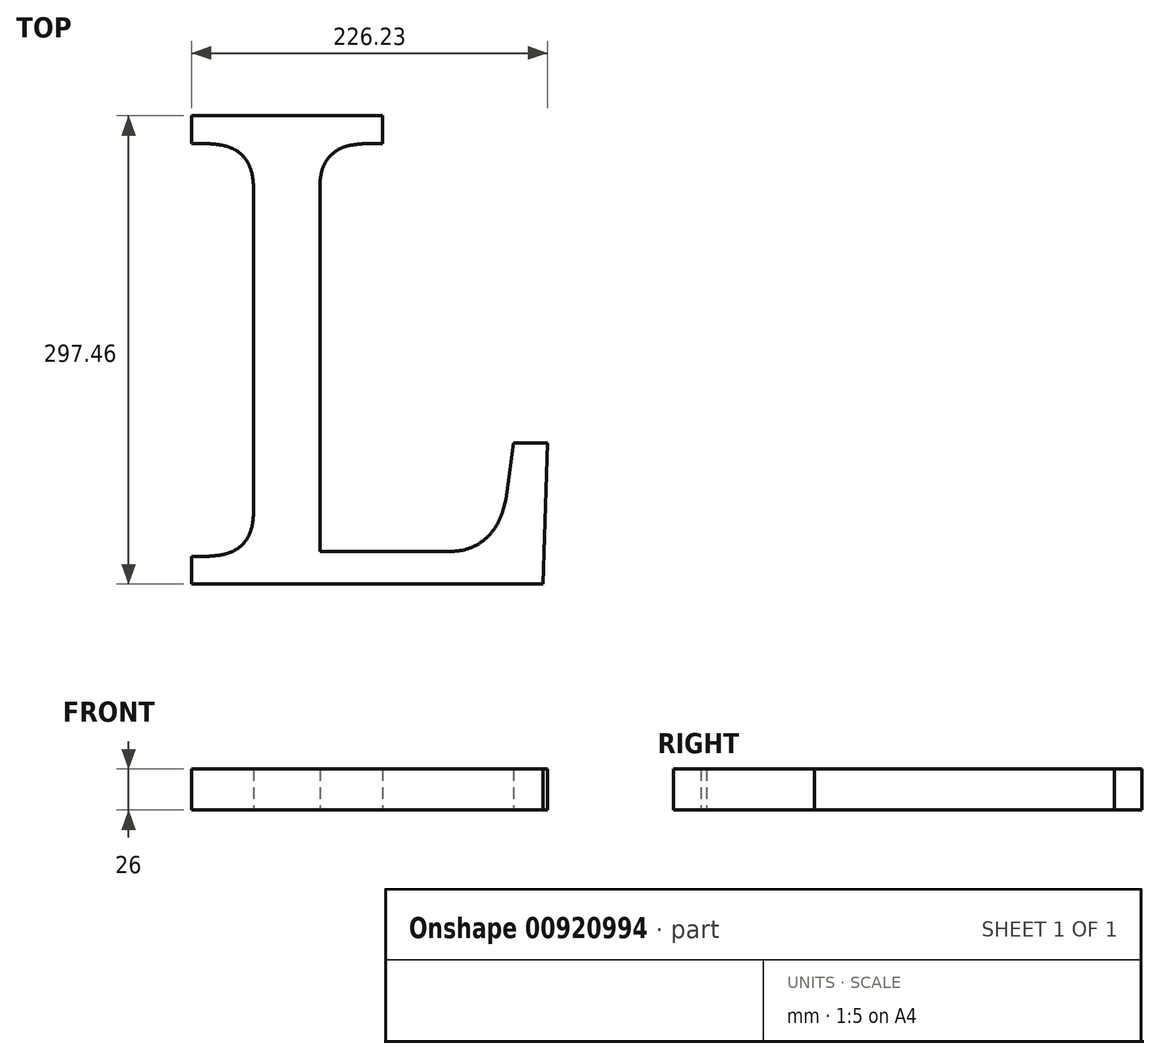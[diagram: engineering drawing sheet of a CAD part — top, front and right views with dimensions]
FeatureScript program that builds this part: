
annotation { "Feature Type Name" : "Feature", "Feature Type Description" : "" }
export const myFeature = defineFeature(function(context is Context, id is Id, definition is map)
    precondition{}
    {
        {
            var Q0;
            Q0=qCreatedBy(makeId("Top.planeOp"),FACE);
            var sketch = newSketch(context, id + "F0", { "sketchPlane" : qUnion([Q0])});
            skText(sketch, "E0", { "text": "L", "fontName": "NotoSerif-Regular.ttf"});
            const initialGuessF0  = {"E0": [-0.18333, -0.16067, 1, 0, 0.3]};
            skSetInitialGuess(sketch, initialGuessF0);
            skSolve(sketch);
        }
        {
            var Q0;
            Q0=makeQuery(id+"F0.imprint","IMPRINT",FACE,{"disambiguationData":[TD([[makeQuery(id+"F0.imprint","IMPRINT",EDGE,{"derivedFrom":sQuery(id+"F0.wireOp",EDGE,"E0.sketch_text.stroke-0")}),-1.0]])]});
            extrude(context, id + "F1", {"entities" : qUnion([Q0]), "depth" : 26 * mm, "offsetDistance" : 25 * mm});
        }
    });
